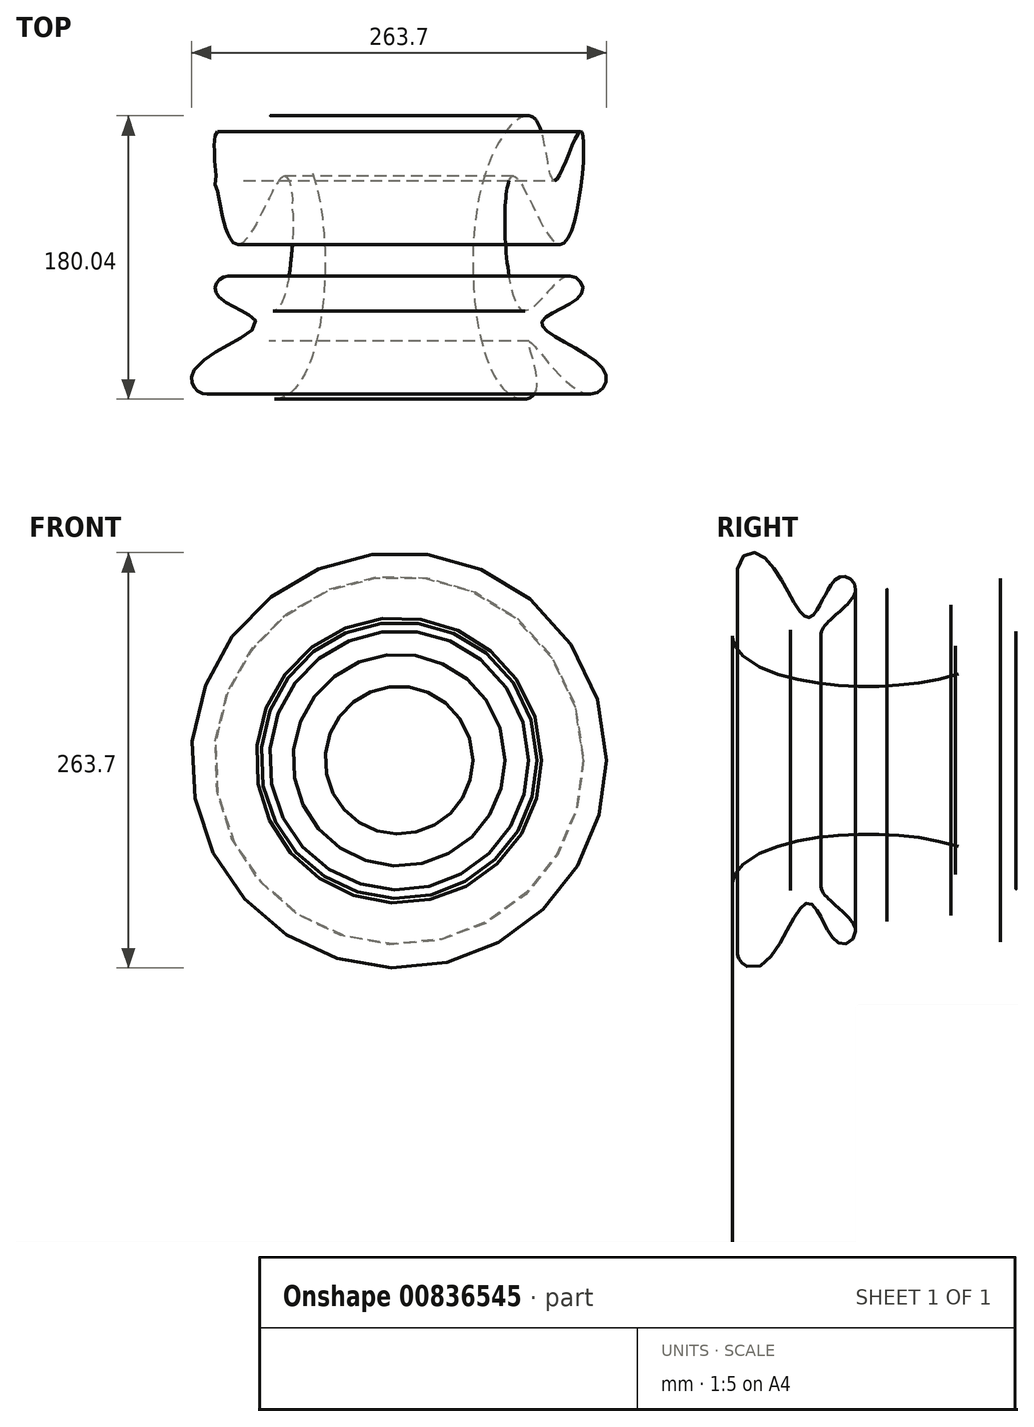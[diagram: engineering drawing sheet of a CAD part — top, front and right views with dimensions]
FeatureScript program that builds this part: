
annotation { "Feature Type Name" : "Feature", "Feature Type Description" : "" }
export const myFeature = defineFeature(function(context is Context, id is Id, definition is map)
    precondition{}
    {
        {
            var Q0;
            Q0=qCreatedBy(makeId("Top.planeOp"),FACE);
            var sketch = newSketch(context, id + "F0", { "sketchPlane" : qUnion([Q0])});
            skFitSpline(sketch, "E0", {"points": [v(54.82, 57.56) * mm, v(67.47, -80.67) * mm, v(87.22, -80.05) * mm, v(82.53, -49.2) * mm, v(119, -82.52) * mm, v(130.88, -68.64) * mm, v(90.61, -37.78) * mm, v(116.22, -18.34) * mm, v(106.66, -8) * mm, v(77.8, -29.14) * mm, v(72.41, 55.7) * mm, v(102.96, 12.2) * mm, v(115.6, 84.09) * mm, v(99.09, 52.93) * mm, v(86.91, 91.5) * mm, v(54.82, 57.56) * mm]});
            skSolve(sketch);
        }
        {
            var Q0;
            Q0=qCreatedBy(makeId("Top.planeOp"),FACE);
            var sketch = newSketch(context, id + "F1", { "sketchPlane" : qUnion([Q0])});
            skLineSegment(sketch, "E1", {"start": v(0, 439.6) * mm, "end": v(0, 230.87) * mm});
            skSolve(sketch);
        }
        {
            var Q0;
            Q0=makeQuery(id+"F0.imprint","IMPRINT",FACE,{"disambiguationData":[TD([[makeQuery(id+"F0.imprint","IMPRINT",EDGE,{"derivedFrom":sQuery(id+"F0.wireOp",EDGE,"E0")}),1.0]])]});
            var Q1;
            Q1=sQuery(id+"F1.wireOp",EDGE,"E1");
            revolve(context, id + "F2", {"surfaceOperationType" : NewSurfaceOperationType.NEW, "entities" : qUnion([Q0]), "axis" : qUnion([Q1]), "revolveType" : RevolveType.FULL});
        }
    });
